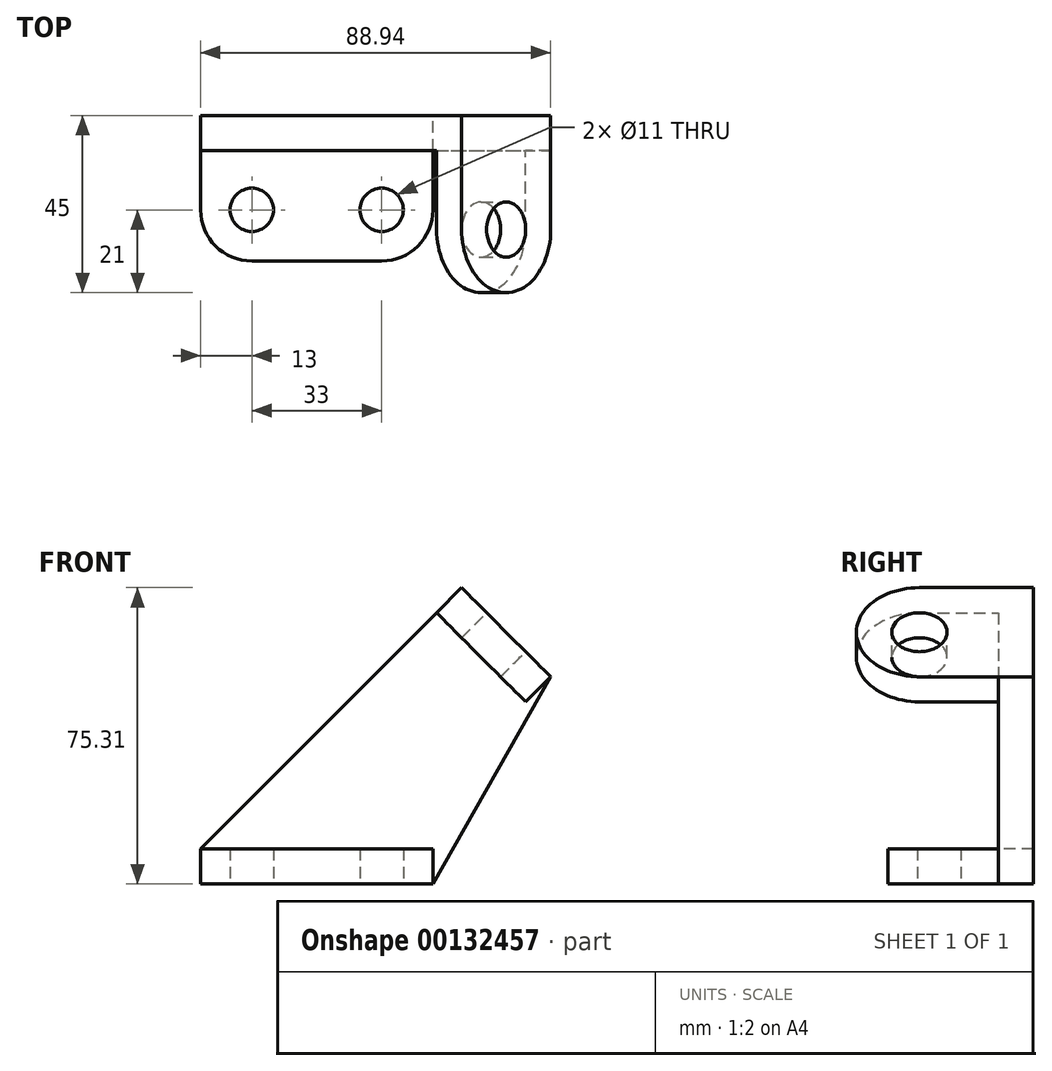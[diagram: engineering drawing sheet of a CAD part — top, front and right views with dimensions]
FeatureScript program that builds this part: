
annotation { "Feature Type Name" : "Feature", "Feature Type Description" : "" }
export const myFeature = defineFeature(function(context is Context, id is Id, definition is map)
    precondition{}
    {
        {
            var Q0;
            Q0=qCreatedBy(makeId("Top.planeOp"),FACE);
            var sketch = newSketch(context, id + "F0", { "sketchPlane" : qUnion([Q0])});
            skLineSegment(sketch, "E0", {"start": v(0, 0) * mm, "end": v(0, -24) * mm});
            skArc(sketch, "E1", {"start": v(0, -24) * mm, "mid": v(3.8, -33.2) * mm, "end": v(13, -37) * mm});
            skLineSegment(sketch, "E2", {"start": v(13, -37) * mm, "end": v(46, -37) * mm});
            skArc(sketch, "E3", {"start": v(46, -37) * mm, "mid": v(55.2, -33.2) * mm, "end": v(59, -24) * mm});
            skLineSegment(sketch, "E4", {"start": v(59, -24) * mm, "end": v(59, 0) * mm});
            skLineSegment(sketch, "E5", {"start": v(0, 0) * mm, "end": v(59, 0) * mm});
            skCircle(sketch, "E6", {"center": v(13, -24) * mm, "radius": 5.5 * mm});
            skCircle(sketch, "E7", {"center": v(46, -24) * mm, "radius": 5.5 * mm});
            skSolve(sketch);
        }
        {
            var Q0;
            Q0 = qSketchRegion(id + "F0", true);
            extrude(context, id + "F1", {"entities" : qUnion([Q0]), "depth" : 9 * mm});
        }
        {
            var Q0;
            Q0=makeQuery(id+"F1.opExtrude","SWEPT_FACE",FACE,{"disambiguationData":[OSD([sQuery(id+"F0.wireOp",EDGE,"E5")])]});
            var sketch = newSketch(context, id + "F2", { "sketchPlane" : qUnion([Q0])});
            skLineSegment(sketch, "E8", {"start": v(-59, 0) * mm, "end": v(-88.94, 52.69) * mm});
            skLineSegment(sketch, "E9", {"start": v(-88.94, 52.69) * mm, "end": v(-66.31, 75.31) * mm});
            skLineSegment(sketch, "E10", {"start": v(-66.31, 75.31) * mm, "end": v(0, 9) * mm});
            skLineSegment(sketch, "E11", {"start": v(0, 9) * mm, "end": v(0, 0) * mm});
            skLineSegment(sketch, "E12", {"start": v(0, 0) * mm, "end": v(-59, 0) * mm});
            skPoint(sketch, "E13", {"position": v(-77.63, 64) * mm});
            skSolve(sketch);
        }
        {
            var Q0;
            Q0 = qSketchRegion(id + "F2", true);
            extrude(context, id + "F3", {"entities" : qUnion([Q0]), "operationType" : NewBodyOperationType.ADD, "oppositeDirection" : true, "depth" : 9 * mm});
        }
        {
            var Q0;
            Q0=makeQuery(id+"F3.opExtrude","SWEPT_FACE",FACE,{"disambiguationData":[OSD([sQuery(id+"F2.wireOp",EDGE,"E9")])]});
            var sketch = newSketch(context, id + "F4", { "sketchPlane" : qUnion([Q0])});
            skPoint(sketch, "E14.oppositeSnap0", {"position": v(-4.5, -25.64) * mm});
            skLineSegment(sketch, "E14.bottom", {"start": v(0, 6.36) * mm, "end": v(-29, 6.36) * mm});
            skLineSegment(sketch, "E14.top", {"start": v(0, -25.64) * mm, "end": v(-29, -25.64) * mm});
            skLineSegment(sketch, "E14.left", {"start": v(0, 6.36) * mm, "end": v(0, -25.64) * mm});
            skArc(sketch, "E15", {"start": v(-29, 6.36) * mm, "mid": v(-45, -9.64) * mm, "end": v(-29, -25.64) * mm});
            skCircle(sketch, "E16", {"center": v(-29, -9.64) * mm, "radius": 7 * mm});
            skSolve(sketch);
        }
        {
            var Q0;
            Q0 = qSketchRegion(id + "F4", true);
            extrude(context, id + "F5", {"entities" : qUnion([Q0]), "operationType" : NewBodyOperationType.ADD, "oppositeDirection" : true, "depth" : 9 * mm});
        }
    });
